# Revit family: 2093145 Sylvania Lighting Fixture MC2-KIT 2-4M 4K DALI WHT PROS
name_source: partatom
category: Lighting Fixtures
revit_build: Autodesk Revit 2016 (Build: 20150220_1215(x64)
units: mm (PartAtom-declared; Revit-internal decimal feet)

## family parameters
Cut with Voids When Loaded = No
Host = Face
Light Source = Yes
OmniClass Number = 23.80.70.11.17
OmniClass Title = Specialized Lighting by Location or Use
Part Type = Normal
Room Calculation Point = No
Round Connector Dimension = Use Diameter
Shared = No

## types (1)
- 2093145 MC2-KIT 2.4M 4K DALI WHT PRIS
    Apparent Load = 42 VA
    Assembly Code = D5020200
    AssetType = Fixed
    Color Filter = 16777215
    Default Elevation = 0 mm  [stored 0 ft]
    Description = 2093145   MC2-KIT 2.4M 4K DALI WHT PRIS  Continuous lines of LED light, white RAL 9016, direct distribution, suspended kit version is pre-wired and supplied complete with end caps and suspension cables, compact and minimalist design based on the Golden Mean, ideal for offices, meeting rooms, corridors, education facilities, museums and libraries, extruded aluminium body, diffuser: micro prismatic, colour temperature: 4000K neutral white, total system power: 42W, total fixture output: 4190lm, luminaire efficacy: 100lm/W, LOR: 100%, colour rendering: Ra >80, LED Chromacity: 1 step MacAdam ellipse, lifetime: 60,000 hours at 90% of the original output (L90), energy class: A++, A+, A, IR/UV free light source without heat radiation, operating voltage: 220-240V / 50-60Hz, drive current: 800mA, electronic driver, DALI dimmable, electrical protection: CLASS I, IP20, suitable for internal environment only.
    Dimming Lamp Color Temperature Shift = <None>
    DocumentationLiterature = http://www.sylvania-lighting.com
    DurationUnit = hours
    ElectricShockClassification = Class I
    Emit Shape Visible in Rendering = No
    Emit from Rectangle Length = 2400 mm
    Emit from Rectangle Width = 52 mm  [stored 0.170604 ft]
    ExpectedLife = 50000
    Height_SYL = 86 mm
    IfcExportAs = IfcLightFixtureType
    IfcExportType = IfcLightFixtureType
    IngressProtection = IP20
    Keynote = 16500
    Lamp = LED
    LampColourRenderingIndex = 80
    LampColourTemperature = 4000 K
    LampMacAdamStep = 3
    LampNominalLuminous = 4442 lm
    LampsType = LED
    Length_SYL = 2400 mm
    LightOutputRatio = 100
    LuminousEfficacy = 106 lm/W
    Manufacturer = Feilo Sylvania
    ManufacturerName = Feilo Sylvania
    Material = aluminium housing, polycarbonate diffuser
    Material_1_SYL = Metal_Sylvania_Mini Continuum II_White
    Material_2_SYL = Polycarbonate_Sylvania_Mini Continuum II_Opal_4000K
    Material_3_SYL = Metal_Sylvania_Mini Contiuum II_Silver
    Material_4_SYL = Metal_Sylvania_Mini Contiuum II_Silver
    Model = MC2-KIT 2.4M 4K DALI WHT PRIS
    ModelNumber = 2093145
    ModelReference = MC2-KIT 2.4M 4K DALI WHT PRIS
    Name = MC2-KIT 2.4M 4K DALI WHT PRIS
    NominalHeight = 86 mm
    NominalLength = 2400 mm
    NominalWidth = 0 mm  [stored 0 ft]
    Photometric Web File = 2093145.ies
    PowerConsumption = 42 W
    PowerFactor = 0.98
    Tilt Angle = -90.00°
    TypeName = MC2-KIT 2.4M 4K DALI WHT PRIS
    URL = http://www.sylvania-lighting.com
    Voltage = 0 V
    Weight = 6.3 kg
    Width_SYL = 54 mm

note: [stored X ft] marks values corroborated as IEEE doubles in the binary element streams (Revit-internal decimal feet)

## geometry (parser evidence)
native form markers: Sweep x3
no freeform markers — native parametric forms only
